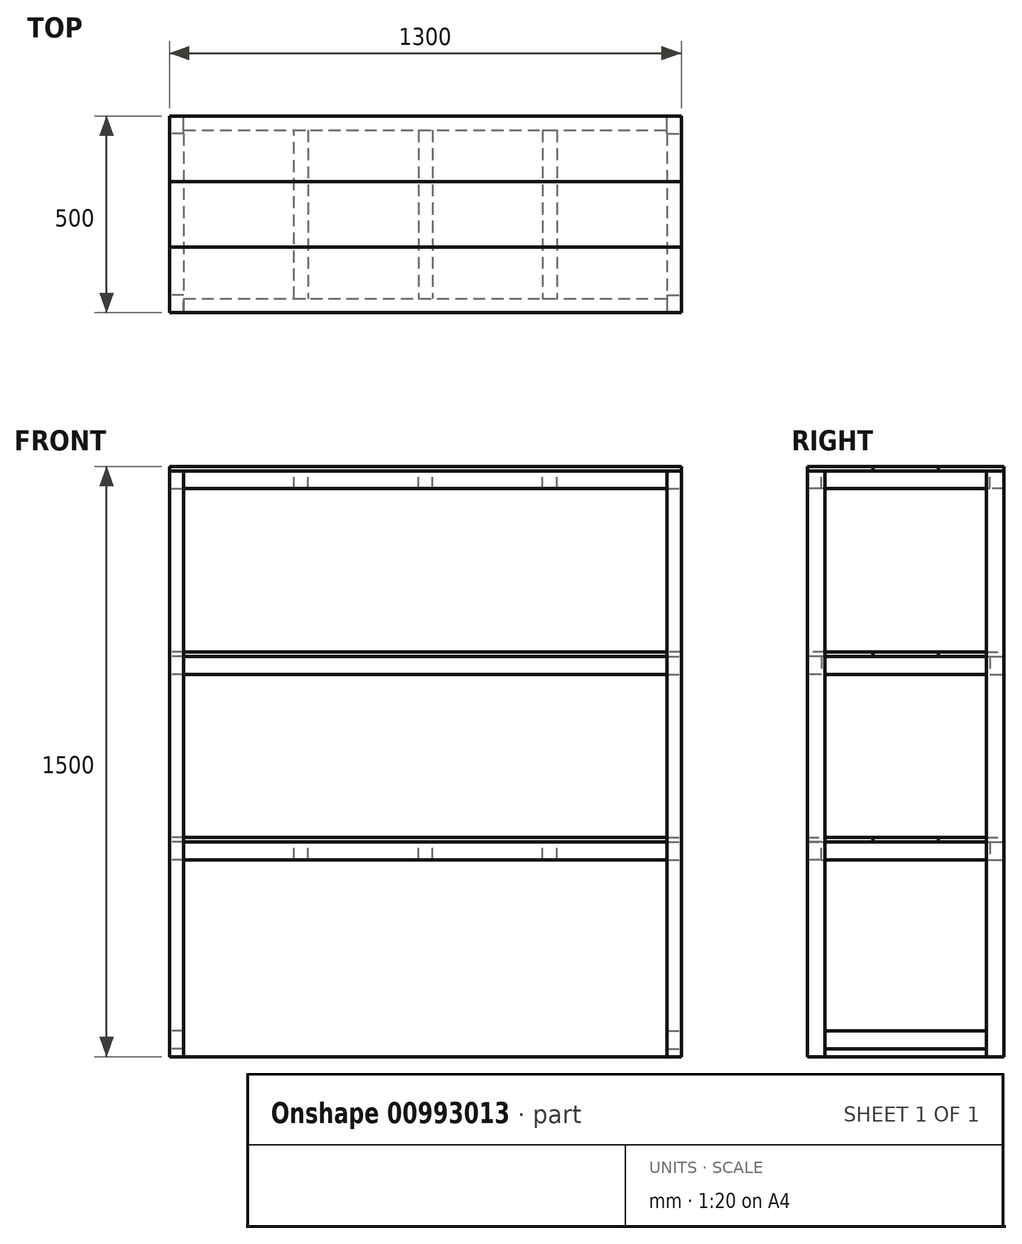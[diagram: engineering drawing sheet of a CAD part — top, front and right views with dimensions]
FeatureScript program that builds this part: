
annotation { "Feature Type Name" : "Feature", "Feature Type Description" : "" }
export const myFeature = defineFeature(function(context is Context, id is Id, definition is map)
    precondition{}
    {
        {
            assignVariable(context, id + "F0", {"name" : "h", "anyValue" : 1500});
        }
        {
            var Q0;
            Q0=qCreatedBy(makeId("Top.planeOp"),FACE);
            var sketch = newSketch(context, id + "F1", { "sketchPlane" : qUnion([Q0])});
            skLineSegment(sketch, "E0.bottom", {"start": v(650, 250) * mm, "end": v(-650, 250) * mm});
            skLineSegment(sketch, "E0.top", {"start": v(650, -250) * mm, "end": v(-650, -250) * mm});
            skLineSegment(sketch, "E0.left", {"start": v(650, 250) * mm, "end": v(650, -250) * mm});
            skLineSegment(sketch, "E0.right", {"start": v(-650, 250) * mm, "end": v(-650, -250) * mm});
            skPoint(sketch, "E0.middle", {"position": v(0, 0) * mm});
            skSolve(sketch);
        }
        {
            var Q0;
            Q0=makeQuery(id+"F1.imprint","IMPRINT",FACE,{"disambiguationData":[TD([[makeQuery(id+"F1.imprint","IMPRINT",EDGE,{"derivedFrom":sQuery(id+"F1.wireOp",EDGE,"E0.bottom")}),1.0]])]});
            extrude(context, id + "F2", {"entities" : qUnion([Q0]), "depth" : (getVariable(context, 'h')) * mm, "offsetDistance" : 25 * mm});
        }
        {
            var Q0;
            Q0=makeQuery(id+"F2.opExtrude","CAP_FACE",FACE,{"disambiguationData":[OSD([sQuery(id+"F1.wireOp",EDGE,"E0.bottom"),sQuery(id+"F1.wireOp",EDGE,"E0.top"),sQuery(id+"F1.wireOp",EDGE,"E0.left"),sQuery(id+"F1.wireOp",EDGE,"E0.right")])],"isStart":false});
            cPlane(context, id + "F3", {"entities" : qUnion([Q0]), "cplaneType" : CPlaneType.OFFSET, "offset" : 12 * mm, "oppositeDirection" : true, "width" : 150 * mm, "height" : 150 * mm});
        }
        {
            var Q0;
            Q0=makeQuery(id+"F2.opExtrude","CAP_FACE",FACE,{"disambiguationData":[OSD([sQuery(id+"F1.wireOp",EDGE,"E0.bottom"),sQuery(id+"F1.wireOp",EDGE,"E0.top"),sQuery(id+"F1.wireOp",EDGE,"E0.left"),sQuery(id+"F1.wireOp",EDGE,"E0.right")])],"isStart":true});
            var sketch = newSketch(context, id + "F4", { "sketchPlane" : qUnion([Q0])});
            skLineSegment(sketch, "E1.bottom", {"start": v(-650, 205) * mm, "end": v(-614, 205) * mm});
            skLineSegment(sketch, "E1.top", {"start": v(-650, 250) * mm, "end": v(-614, 250) * mm});
            skLineSegment(sketch, "E1.left", {"start": v(-650, 205) * mm, "end": v(-650, 250) * mm});
            skLineSegment(sketch, "E1.right", {"start": v(-614, 205) * mm, "end": v(-614, 250) * mm});
            skLineSegment(sketch, "E2.bottom", {"start": v(-650, -250) * mm, "end": v(-614, -250) * mm});
            skLineSegment(sketch, "E2.top", {"start": v(-650, -205) * mm, "end": v(-614, -205) * mm});
            skLineSegment(sketch, "E2.left", {"start": v(-650, -250) * mm, "end": v(-650, -205) * mm});
            skLineSegment(sketch, "E2.right", {"start": v(-614, -250) * mm, "end": v(-614, -205) * mm});
            skLineSegment(sketch, "E3.bottom", {"start": v(650, -250) * mm, "end": v(614, -250) * mm});
            skLineSegment(sketch, "E3.top", {"start": v(650, -205) * mm, "end": v(614, -205) * mm});
            skLineSegment(sketch, "E3.left", {"start": v(650, -250) * mm, "end": v(650, -205) * mm});
            skLineSegment(sketch, "E3.right", {"start": v(614, -250) * mm, "end": v(614, -205) * mm});
            skLineSegment(sketch, "E4.bottom", {"start": v(650, 250) * mm, "end": v(614, 250) * mm});
            skLineSegment(sketch, "E4.top", {"start": v(650, 205) * mm, "end": v(614, 205) * mm});
            skLineSegment(sketch, "E4.left", {"start": v(650, 250) * mm, "end": v(650, 205) * mm});
            skLineSegment(sketch, "E4.right", {"start": v(614, 250) * mm, "end": v(614, 205) * mm});
            skSolve(sketch);
        }
        {
            var Q0;
            Q0=makeQuery(id+"F4.imprint","IMPRINT",FACE,{"disambiguationData":[TD([[makeQuery(id+"F4.imprint","IMPRINT",EDGE,{"derivedFrom":sQuery(id+"F4.wireOp",EDGE,"E1.bottom")}),1.0]])]});
            var Q1;
            Q1=makeQuery(id+"F4.imprint","IMPRINT",FACE,{"disambiguationData":[TD([[makeQuery(id+"F4.imprint","IMPRINT",EDGE,{"derivedFrom":sQuery(id+"F4.wireOp",EDGE,"E2.bottom")}),-1.0]])]});
            var Q2;
            Q2=makeQuery(id+"F4.imprint","IMPRINT",FACE,{"disambiguationData":[TD([[makeQuery(id+"F4.imprint","IMPRINT",EDGE,{"derivedFrom":sQuery(id+"F4.wireOp",EDGE,"E4.bottom")}),1.0]])]});
            var Q3;
            Q3=makeQuery(id+"F4.imprint","IMPRINT",FACE,{"disambiguationData":[TD([[makeQuery(id+"F4.imprint","IMPRINT",EDGE,{"derivedFrom":sQuery(id+"F4.wireOp",EDGE,"E3.bottom")}),-1.0]])]});
            var Q4;
            Q4=qCreatedBy(id+"F3.planeOp",FACE);
            extrude(context, id + "F5", {"entities" : qUnion([Q0, Q1, Q2, Q3]), "endBound" : BoundingType.UP_TO_SURFACE, "oppositeDirection" : true, "depth" : (getVariable(context, 'h') - 12) * mm, "endBoundEntityFace" : qUnion([Q4]), "offsetDistance" : 25 * mm});
        }
        {
            var Q0;
            Q0=qCreatedBy(id+"F3.planeOp",FACE);
            var sketch = newSketch(context, id + "F6", { "sketchPlane" : qUnion([Q0])});
            skLineSegment(sketch, "E5.bottom", {"start": v(-650, 205) * mm, "end": v(-614, 205) * mm});
            skLineSegment(sketch, "E5.top", {"start": v(-650, -205) * mm, "end": v(-614, -205) * mm});
            skLineSegment(sketch, "E5.left", {"start": v(-650, 205) * mm, "end": v(-650, -205) * mm});
            skLineSegment(sketch, "E5.right", {"start": v(-614, 205) * mm, "end": v(-614, -205) * mm});
            skLineSegment(sketch, "E6.bottom", {"start": v(-614, 250) * mm, "end": v(614, 250) * mm});
            skLineSegment(sketch, "E6.top", {"start": v(-614, 214) * mm, "end": v(614, 214) * mm});
            skLineSegment(sketch, "E6.left", {"start": v(-614, 250) * mm, "end": v(-614, 214) * mm});
            skLineSegment(sketch, "E6.right", {"start": v(614, 250) * mm, "end": v(614, 214) * mm});
            skLineSegment(sketch, "E7.bottom", {"start": v(614, 205) * mm, "end": v(650, 205) * mm});
            skLineSegment(sketch, "E7.top", {"start": v(614, -205) * mm, "end": v(650, -205) * mm});
            skLineSegment(sketch, "E7.left", {"start": v(614, 205) * mm, "end": v(614, -205) * mm});
            skLineSegment(sketch, "E7.right", {"start": v(650, 205) * mm, "end": v(650, -205) * mm});
            skLineSegment(sketch, "E8.bottom", {"start": v(-614, -214) * mm, "end": v(614, -214) * mm});
            skLineSegment(sketch, "E8.top", {"start": v(-614, -250) * mm, "end": v(614, -250) * mm});
            skLineSegment(sketch, "E8.left", {"start": v(-614, -214) * mm, "end": v(-614, -250) * mm});
            skLineSegment(sketch, "E8.right", {"start": v(614, -214) * mm, "end": v(614, -250) * mm});
            skSolve(sketch);
        }
        {
            var Q0;
            Q0=makeQuery(id+"F6.imprint","IMPRINT",FACE,{"disambiguationData":[TD([[makeQuery(id+"F6.imprint","IMPRINT",EDGE,{"derivedFrom":sQuery(id+"F6.wireOp",EDGE,"E5.bottom")}),-1.0]])]});
            var Q1;
            Q1=makeQuery(id+"F6.imprint","IMPRINT",FACE,{"disambiguationData":[TD([[makeQuery(id+"F6.imprint","IMPRINT",EDGE,{"derivedFrom":sQuery(id+"F6.wireOp",EDGE,"E6.bottom")}),-1.0]])]});
            var Q2;
            Q2=makeQuery(id+"F6.imprint","IMPRINT",FACE,{"disambiguationData":[TD([[makeQuery(id+"F6.imprint","IMPRINT",EDGE,{"derivedFrom":sQuery(id+"F6.wireOp",EDGE,"E7.bottom")}),-1.0]])]});
            var Q3;
            Q3=makeQuery(id+"F6.imprint","IMPRINT",FACE,{"disambiguationData":[TD([[makeQuery(id+"F6.imprint","IMPRINT",EDGE,{"derivedFrom":sQuery(id+"F6.wireOp",EDGE,"E8.bottom")}),-1.0]])]});
            extrude(context, id + "F7", {"entities" : qUnion([Q0, Q1, Q2, Q3]), "oppositeDirection" : true, "depth" : 45 * mm, "offsetDistance" : 25 * mm});
        }
        {
            var Q0;
            Q0=qCreatedBy(id+"F3.planeOp",FACE);
            var sketch = newSketch(context, id + "F8", { "sketchPlane" : qUnion([Q0])});
            skLineSegment(sketch, "E9.bottom", {"start": v(-334, 214) * mm, "end": v(-298, 214) * mm});
            skLineSegment(sketch, "E9.top", {"start": v(-334, -214) * mm, "end": v(-298, -214) * mm});
            skLineSegment(sketch, "E9.left", {"start": v(-334, 214) * mm, "end": v(-334, -214) * mm});
            skLineSegment(sketch, "E9.right", {"start": v(-298, 214) * mm, "end": v(-298, -214) * mm});
            skLineSegment(sketch, "E10.bottom", {"start": v(-18, 214) * mm, "end": v(18, 214) * mm});
            skLineSegment(sketch, "E10.top", {"start": v(-18, -214) * mm, "end": v(18, -214) * mm});
            skLineSegment(sketch, "E10.left", {"start": v(-18, 214) * mm, "end": v(-18, -214) * mm});
            skLineSegment(sketch, "E10.right", {"start": v(18, 214) * mm, "end": v(18, -214) * mm});
            skLineSegment(sketch, "E11.bottom", {"start": v(298, 214) * mm, "end": v(334, 214) * mm});
            skLineSegment(sketch, "E11.top", {"start": v(298, -214) * mm, "end": v(334, -214) * mm});
            skLineSegment(sketch, "E11.left", {"start": v(298, 214) * mm, "end": v(298, -214) * mm});
            skLineSegment(sketch, "E11.right", {"start": v(334, 214) * mm, "end": v(334, -214) * mm});
            skSolve(sketch);
        }
        {
            var Q0;
            Q0=makeQuery(id+"F8.imprint","IMPRINT",FACE,{"disambiguationData":[TD([[makeQuery(id+"F8.imprint","IMPRINT",EDGE,{"derivedFrom":sQuery(id+"F8.wireOp",EDGE,"E9.bottom")}),-1.0]])]});
            var Q1;
            Q1=makeQuery(id+"F8.imprint","IMPRINT",FACE,{"disambiguationData":[TD([[makeQuery(id+"F8.imprint","IMPRINT",EDGE,{"derivedFrom":sQuery(id+"F8.wireOp",EDGE,"E10.bottom")}),-1.0]])]});
            var Q2;
            Q2=makeQuery(id+"F8.imprint","IMPRINT",FACE,{"disambiguationData":[TD([[makeQuery(id+"F8.imprint","IMPRINT",EDGE,{"derivedFrom":sQuery(id+"F8.wireOp",EDGE,"E11.bottom")}),-1.0]])]});
            extrude(context, id + "F9", {"entities" : qUnion([Q0, Q1, Q2]), "oppositeDirection" : true, "depth" : 45 * mm, "offsetDistance" : 25 * mm});
        }
        {
            var Q0;
            Q0=makeQuery(id+"F2.opExtrude","CAP_FACE",FACE,{"disambiguationData":[OSD([sQuery(id+"F1.wireOp",EDGE,"E0.bottom"),sQuery(id+"F1.wireOp",EDGE,"E0.top"),sQuery(id+"F1.wireOp",EDGE,"E0.left"),sQuery(id+"F1.wireOp",EDGE,"E0.right")])],"isStart":false});
            var sketch = newSketch(context, id + "F10", { "sketchPlane" : qUnion([Q0])});
            skLineSegment(sketch, "E12.bottom", {"start": v(-650, -83.33) * mm, "end": v(650, -83.33) * mm});
            skLineSegment(sketch, "E12.top", {"start": v(-650, -250) * mm, "end": v(650, -250) * mm});
            skLineSegment(sketch, "E12.left", {"start": v(-650, -83.33) * mm, "end": v(-650, -250) * mm});
            skLineSegment(sketch, "E12.right", {"start": v(650, -83.33) * mm, "end": v(650, -250) * mm});
            skLineSegment(sketch, "E13", {"start": v(-650, -83.33) * mm, "end": v(-650, 83.33) * mm});
            skLineSegment(sketch, "E14", {"start": v(-650, 83.33) * mm, "end": v(650, 83.33) * mm});
            skLineSegment(sketch, "E15", {"start": v(650, 83.33) * mm, "end": v(650, -83.33) * mm});
            skLineSegment(sketch, "E16", {"start": v(-650, 83.33) * mm, "end": v(-650, 250) * mm});
            skLineSegment(sketch, "E17", {"start": v(-650, 250) * mm, "end": v(650, 250) * mm});
            skLineSegment(sketch, "E18", {"start": v(650, 250) * mm, "end": v(650, 83.33) * mm});
            skSolve(sketch);
        }
        {
            var Q0;
            Q0=makeQuery(id+"F10.imprint","IMPRINT",FACE,{"disambiguationData":[TD([[makeQuery(id+"F10.imprint","IMPRINT",EDGE,{"derivedFrom":sQuery(id+"F10.wireOp",EDGE,"E12.bottom")}),-1.0]])]});
            extrude(context, id + "F11", {"entities" : qUnion([Q0]), "oppositeDirection" : true, "depth" : 12 * mm, "offsetDistance" : 25 * mm});
        }
        {
            var Q0;
            Q0=makeQuery(id+"F10.imprint","IMPRINT",FACE,{"disambiguationData":[TD([[makeQuery(id+"F10.imprint","IMPRINT",EDGE,{"derivedFrom":sQuery(id+"F10.wireOp",EDGE,"E12.bottom")}),1.0]])]});
            extrude(context, id + "F12", {"entities" : qUnion([Q0]), "oppositeDirection" : true, "depth" : 12 * mm, "offsetDistance" : 25 * mm});
        }
        {
            var Q0;
            Q0=makeQuery(id+"F10.imprint","IMPRINT",FACE,{"disambiguationData":[TD([[makeQuery(id+"F10.imprint","IMPRINT",EDGE,{"derivedFrom":sQuery(id+"F10.wireOp",EDGE,"E14")}),1.0]])]});
            extrude(context, id + "F13", {"entities" : qUnion([Q0]), "oppositeDirection" : true, "depth" : 12 * mm, "offsetDistance" : 25 * mm});
        }
        {
            var Q0;
            Q0=makeQuery(id+"F2.opExtrude","SWEPT_FACE",FACE,{"disambiguationData":[OSD([sQuery(id+"F1.wireOp",EDGE,"E0.top")])]});
            var sketch = newSketch(context, id + "F14", { "sketchPlane" : qUnion([Q0])});
            skLineSegment(sketch, "E19.bottom", {"start": v(-614, 545) * mm, "end": v(614, 545) * mm});
            skLineSegment(sketch, "E19.top", {"start": v(-614, 500) * mm, "end": v(614, 500) * mm});
            skLineSegment(sketch, "E19.left", {"start": v(-614, 545) * mm, "end": v(-614, 500) * mm});
            skLineSegment(sketch, "E19.right", {"start": v(614, 545) * mm, "end": v(614, 500) * mm});
            skSolve(sketch);
        }
        {
            var Q0;
            Q0=makeQuery(id+"F14.imprint","IMPRINT",FACE,{"disambiguationData":[TD([[makeQuery(id+"F14.imprint","IMPRINT",EDGE,{"derivedFrom":sQuery(id+"F14.wireOp",EDGE,"E19.bottom")}),-1.0]])]});
            extrude(context, id + "F15", {"entities" : qUnion([Q0]), "oppositeDirection" : true, "depth" : 36 * mm, "offsetDistance" : 25 * mm});
        }
        {
            var Q0;
            Q0=makeQuery(id+"F15.opExtrude","SWEPT_BODY",BODY,{"disambiguationData":[OSD([sQuery(id+"F14.wireOp",EDGE,"E19.bottom"),sQuery(id+"F14.wireOp",EDGE,"E19.top"),sQuery(id+"F14.wireOp",EDGE,"E19.left"),sQuery(id+"F14.wireOp",EDGE,"E19.right")])]});
            var Q1;
            Q1=qCreatedBy(makeId("Front.planeOp"),FACE);
            mirror(context, id + "F16", {"entities" : qUnion([Q0]), "mirrorPlane" : qUnion([Q1])});
        }
        {
            var Q0;
            Q0=makeQuery(id+"F2.opExtrude","SWEPT_FACE",FACE,{"disambiguationData":[OSD([sQuery(id+"F1.wireOp",EDGE,"E0.right")])]});
            var sketch = newSketch(context, id + "F17", { "sketchPlane" : qUnion([Q0])});
            skLineSegment(sketch, "E20.bottom", {"start": v(-205, 545) * mm, "end": v(205, 545) * mm});
            skLineSegment(sketch, "E20.top", {"start": v(-205, 500) * mm, "end": v(205, 500) * mm});
            skLineSegment(sketch, "E20.left", {"start": v(-205, 545) * mm, "end": v(-205, 500) * mm});
            skLineSegment(sketch, "E20.right", {"start": v(205, 545) * mm, "end": v(205, 500) * mm});
            skLineSegment(sketch, "E21.0", {"start": v(214, 500) * mm, "end": v(250, 500) * mm});
            skSolve(sketch);
        }
        {
            var Q0;
            Q0=makeQuery(id+"F17.imprint","IMPRINT",FACE,{"disambiguationData":[TD([[makeQuery(id+"F17.imprint","IMPRINT",EDGE,{"derivedFrom":sQuery(id+"F17.wireOp",EDGE,"E20.bottom")}),-1.0]])]});
            extrude(context, id + "F18", {"entities" : qUnion([Q0]), "oppositeDirection" : true, "depth" : 36 * mm, "offsetDistance" : 25 * mm});
        }
        {
            var Q0;
            Q0=makeQuery(id+"F18.opExtrude","SWEPT_BODY",BODY,{"disambiguationData":[OSD([sQuery(id+"F17.wireOp",EDGE,"E20.bottom"),sQuery(id+"F17.wireOp",EDGE,"E20.top"),sQuery(id+"F17.wireOp",EDGE,"E20.left"),sQuery(id+"F17.wireOp",EDGE,"E20.right")])]});
            var Q1;
            Q1=qCreatedBy(makeId("Right.planeOp"),FACE);
            mirror(context, id + "F19", {"entities" : qUnion([Q0]), "mirrorPlane" : qUnion([Q1])});
        }
        {
            var Q0;
            Q0=makeQuery(id+"F15.opExtrude","SWEPT_FACE",FACE,{"disambiguationData":[OSD([sQuery(id+"F14.wireOp",EDGE,"E19.bottom")])]});
            var sketch = newSketch(context, id + "F20", { "sketchPlane" : qUnion([Q0])});
            skLineSegment(sketch, "E22.0.0", {"start": v(-334, -214) * mm, "end": v(-334, 214) * mm});
            skLineSegment(sketch, "E22.0.1", {"start": v(-334, 214) * mm, "end": v(-298, 214) * mm});
            skLineSegment(sketch, "E22.0.2", {"start": v(-298, 214) * mm, "end": v(-298, -214) * mm});
            skLineSegment(sketch, "E22.0.3", {"start": v(-298, -214) * mm, "end": v(-334, -214) * mm});
            skLineSegment(sketch, "E23.0.0", {"start": v(-18, -214) * mm, "end": v(-18, 214) * mm});
            skLineSegment(sketch, "E23.0.1", {"start": v(-18, 214) * mm, "end": v(18, 214) * mm});
            skLineSegment(sketch, "E23.0.2", {"start": v(18, 214) * mm, "end": v(18, -214) * mm});
            skLineSegment(sketch, "E23.0.3", {"start": v(18, -214) * mm, "end": v(-18, -214) * mm});
            skLineSegment(sketch, "E24.0.0", {"start": v(298, -214) * mm, "end": v(298, 214) * mm});
            skLineSegment(sketch, "E24.0.1", {"start": v(298, 214) * mm, "end": v(334, 214) * mm});
            skLineSegment(sketch, "E24.0.2", {"start": v(334, 214) * mm, "end": v(334, -214) * mm});
            skLineSegment(sketch, "E24.0.3", {"start": v(334, -214) * mm, "end": v(298, -214) * mm});
            skSolve(sketch);
        }
        {
            var Q0;
            Q0=makeQuery(id+"F20.imprint","IMPRINT",FACE,{"disambiguationData":[TD([[makeQuery(id+"F20.imprint","IMPRINT",EDGE,{"derivedFrom":sQuery(id+"F20.wireOp",EDGE,"E22.0.0")}),-1.0]])]});
            var Q1;
            Q1=makeQuery(id+"F20.imprint","IMPRINT",FACE,{"disambiguationData":[TD([[makeQuery(id+"F20.imprint","IMPRINT",EDGE,{"derivedFrom":sQuery(id+"F20.wireOp",EDGE,"E23.0.0")}),-1.0]])]});
            var Q2;
            Q2=makeQuery(id+"F20.imprint","IMPRINT",FACE,{"disambiguationData":[TD([[makeQuery(id+"F20.imprint","IMPRINT",EDGE,{"derivedFrom":sQuery(id+"F20.wireOp",EDGE,"E24.0.0")}),-1.0]])]});
            extrude(context, id + "F21", {"entities" : qUnion([Q0, Q1, Q2]), "oppositeDirection" : true, "depth" : 45 * mm, "offsetDistance" : 25 * mm});
        }
        {
            var Q0;
            Q0=makeQuery(id+"F15.opExtrude","SWEPT_FACE",FACE,{"disambiguationData":[OSD([sQuery(id+"F14.wireOp",EDGE,"E19.bottom")])]});
            var sketch = newSketch(context, id + "F22", { "sketchPlane" : qUnion([Q0])});
            skLineSegment(sketch, "E25.0.0", {"start": v(650, -83.33) * mm, "end": v(-650, -83.33) * mm});
            skLineSegment(sketch, "E25.0.1", {"start": v(-650, -83.33) * mm, "end": v(-650, -250) * mm});
            skLineSegment(sketch, "E25.0.2", {"start": v(-650, -250) * mm, "end": v(650, -250) * mm});
            skLineSegment(sketch, "E25.0.3", {"start": v(650, -250) * mm, "end": v(650, -83.33) * mm});
            skLineSegment(sketch, "E26.0.0", {"start": v(650, 83.33) * mm, "end": v(-650, 83.33) * mm});
            skLineSegment(sketch, "E26.0.1", {"start": v(-650, 83.33) * mm, "end": v(-650, -83.33) * mm});
            skLineSegment(sketch, "E26.0.2", {"start": v(-650, -83.33) * mm, "end": v(650, -83.33) * mm});
            skLineSegment(sketch, "E26.0.3", {"start": v(650, -83.33) * mm, "end": v(650, 83.33) * mm});
            skLineSegment(sketch, "E27.0.0", {"start": v(-650, 250) * mm, "end": v(-650, 83.33) * mm});
            skLineSegment(sketch, "E27.0.1", {"start": v(-650, 83.33) * mm, "end": v(650, 83.33) * mm});
            skLineSegment(sketch, "E27.0.2", {"start": v(650, 83.33) * mm, "end": v(650, 250) * mm});
            skLineSegment(sketch, "E27.0.3", {"start": v(650, 250) * mm, "end": v(-650, 250) * mm});
            skSolve(sketch);
        }
        {
            var Q0;
            {var subQ5=sQuery(id+"F22.wireOp",EDGE,"E25.0.1");Q0=makeQuery(id+"F22.imprint","IMPRINT",FACE,{"disambiguationData":[TD([[makeQuery(id+"F22.imprint","IMPRINT",EDGE,{"derivedFrom":subQ5}),1.0]])]});}
            var Q1;
            {var subQ1=sQuery(id+"F14.wireOp",EDGE,"E19.bottom");Q1=makeQuery(id+"F22.imprint","IMPRINT",FACE,{"disambiguationData":[TD([[makeQuery(id+"F22.imprint","IMPRINT",EDGE,{"derivedFrom":makeQuery(id+"F15.opExtrude","CAP_EDGE",EDGE,{"disambiguationData":[OSD([subQ1])],"isStart":false})}),-1.0]])]});}
            extrude(context, id + "F23", {"entities" : qUnion([Q0, Q1]), "depth" : 12 * mm, "offsetDistance" : 25 * mm});
        }
        {
            var Q0;
            Q0=makeQuery(id+"F22.imprint","IMPRINT",FACE,{"disambiguationData":[TD([[makeQuery(id+"F22.imprint","IMPRINT",EDGE,{"derivedFrom":sQuery(id+"F22.wireOp",EDGE,"E26.0.1")}),1.0]])]});
            extrude(context, id + "F24", {"entities" : qUnion([Q0]), "depth" : 12 * mm, "offsetDistance" : 25 * mm});
        }
        {
            var Q0;
            Q0=makeQuery(id+"F22.imprint","IMPRINT",FACE,{"disambiguationData":[TD([[makeQuery(id+"F22.imprint","IMPRINT",EDGE,{"derivedFrom":sQuery(id+"F22.wireOp",EDGE,"E27.0.0")}),1.0]])]});
            extrude(context, id + "F25", {"entities" : qUnion([Q0]), "depth" : 12 * mm, "offsetDistance" : 25 * mm});
        }
        {
            var Q0;
            Q0=makeQuery(id+"F5.opExtrude","SWEPT_BODY",BODY,{"disambiguationData":[OSD([sQuery(id+"F4.wireOp",EDGE,"E1.bottom"),sQuery(id+"F4.wireOp",EDGE,"E1.top"),sQuery(id+"F4.wireOp",EDGE,"E1.left"),sQuery(id+"F4.wireOp",EDGE,"E1.right")])]});
            var Q1;
            Q1=makeQuery(id+"F5.opExtrude","SWEPT_BODY",BODY,{"disambiguationData":[OSD([sQuery(id+"F4.wireOp",EDGE,"E4.bottom"),sQuery(id+"F4.wireOp",EDGE,"E4.top"),sQuery(id+"F4.wireOp",EDGE,"E4.left"),sQuery(id+"F4.wireOp",EDGE,"E4.right")])]});
            var Q2;
            Q2=makeQuery(id+"F23.opExtrude","SWEPT_BODY",BODY,{"disambiguationData":[OSD([sQuery(id+"F22.wireOp",EDGE,"E25.0.1"),sQuery(id+"F22.wireOp",EDGE,"E25.0.2"),sQuery(id+"F22.wireOp",EDGE,"E25.0.3"),sQuery(id+"F22.wireOp",EDGE,"E26.0.2")])]});
            booleanBodies(context, id + "F26", {"operationType" : BooleanOperationType.SUBTRACTION, "tools" : qUnion([Q0, Q1]), "targets" : qUnion([Q2]), "keepTools" : true});
        }
        {
            var Q0;
            Q0=makeQuery(id+"F5.opExtrude","SWEPT_BODY",BODY,{"disambiguationData":[OSD([sQuery(id+"F4.wireOp",EDGE,"E2.bottom"),sQuery(id+"F4.wireOp",EDGE,"E2.top"),sQuery(id+"F4.wireOp",EDGE,"E2.left"),sQuery(id+"F4.wireOp",EDGE,"E2.right")])]});
            var Q1;
            Q1=makeQuery(id+"F5.opExtrude","SWEPT_BODY",BODY,{"disambiguationData":[OSD([sQuery(id+"F4.wireOp",EDGE,"E3.bottom"),sQuery(id+"F4.wireOp",EDGE,"E3.top"),sQuery(id+"F4.wireOp",EDGE,"E3.left"),sQuery(id+"F4.wireOp",EDGE,"E3.right")])]});
            var Q2;
            Q2=makeQuery(id+"F25.opExtrude","SWEPT_BODY",BODY,{"disambiguationData":[OSD([sQuery(id+"F22.wireOp",EDGE,"E27.0.0"),sQuery(id+"F22.wireOp",EDGE,"E27.0.1"),sQuery(id+"F22.wireOp",EDGE,"E27.0.2"),sQuery(id+"F22.wireOp",EDGE,"E27.0.3")])]});
            booleanBodies(context, id + "F27", {"operationType" : BooleanOperationType.SUBTRACTION, "tools" : qUnion([Q0, Q1]), "targets" : qUnion([Q2]), "keepTools" : true});
        }
        {
            var Q0;
            Q0=makeQuery(id+"F2.opExtrude","SWEPT_FACE",FACE,{"disambiguationData":[OSD([sQuery(id+"F1.wireOp",EDGE,"E0.right")])]});
            var sketch = newSketch(context, id + "F28", { "sketchPlane" : qUnion([Q0])});
            skLineSegment(sketch, "E28.bottom", {"start": v(-205, 65) * mm, "end": v(205, 65) * mm});
            skLineSegment(sketch, "E28.top", {"start": v(-205, 20) * mm, "end": v(205, 20) * mm});
            skLineSegment(sketch, "E28.left", {"start": v(-205, 65) * mm, "end": v(-205, 20) * mm});
            skLineSegment(sketch, "E28.right", {"start": v(205, 65) * mm, "end": v(205, 20) * mm});
            skSolve(sketch);
        }
        {
            var Q0;
            Q0=makeQuery(id+"F28.imprint","IMPRINT",FACE,{"disambiguationData":[TD([[makeQuery(id+"F28.imprint","IMPRINT",EDGE,{"derivedFrom":sQuery(id+"F28.wireOp",EDGE,"E28.bottom")}),-1.0]])]});
            extrude(context, id + "F29", {"entities" : qUnion([Q0]), "oppositeDirection" : true, "depth" : 36 * mm, "offsetDistance" : 25 * mm});
        }
        {
            var Q0;
            Q0=makeQuery(id+"F29.opExtrude","SWEPT_BODY",BODY,{"disambiguationData":[OSD([sQuery(id+"F28.wireOp",EDGE,"E28.bottom"),sQuery(id+"F28.wireOp",EDGE,"E28.top"),sQuery(id+"F28.wireOp",EDGE,"E28.left"),sQuery(id+"F28.wireOp",EDGE,"E28.right")])]});
            var Q1;
            Q1=qCreatedBy(makeId("Right.planeOp"),FACE);
            mirror(context, id + "F30", {"entities" : qUnion([Q0]), "mirrorPlane" : qUnion([Q1])});
        }
        {
            var Q0;
            Q0=makeQuery(id+"F2.opExtrude","SWEPT_FACE",FACE,{"disambiguationData":[OSD([sQuery(id+"F1.wireOp",EDGE,"E0.top")])]});
            var sketch = newSketch(context, id + "F31", { "sketchPlane" : qUnion([Q0])});
            skLineSegment(sketch, "E29.bottom", {"start": v(-614, 1016.5) * mm, "end": v(614, 1016.5) * mm});
            skLineSegment(sketch, "E29.top", {"start": v(-614, 971.5) * mm, "end": v(614, 971.5) * mm});
            skLineSegment(sketch, "E29.left", {"start": v(-614, 1016.5) * mm, "end": v(-614, 971.5) * mm});
            skLineSegment(sketch, "E29.right", {"start": v(614, 1016.5) * mm, "end": v(614, 971.5) * mm});
            skLineSegment(sketch, "E30", {"start": v(-614, 1016.5) * mm, "end": v(-614, 1028.5) * mm, "construction": true});
            skLineSegment(sketch, "E31", {"start": v(-614, 1028.5) * mm, "end": v(614, 1028.5) * mm, "construction": true});
            skLineSegment(sketch, "E32", {"start": v(614, 1028.5) * mm, "end": v(614, 1016.5) * mm, "construction": true});
            skLineSegment(sketch, "E33", {"start": v(0, 1443) * mm, "end": v(0, 1028.5) * mm, "construction": true});
            skLineSegment(sketch, "E34", {"start": v(0, 971.5) * mm, "end": v(0, 557) * mm, "construction": true});
            skSolve(sketch);
        }
        {
            var Q0;
            Q0=makeQuery(id+"F31.imprint","IMPRINT",FACE,{"disambiguationData":[TD([[makeQuery(id+"F31.imprint","IMPRINT",EDGE,{"derivedFrom":sQuery(id+"F31.wireOp",EDGE,"E29.bottom")}),-1.0]])]});
            extrude(context, id + "F32", {"entities" : qUnion([Q0]), "oppositeDirection" : true, "depth" : 36 * mm, "offsetDistance" : 25 * mm});
        }
        {
            var Q0;
            Q0=makeQuery(id+"F32.opExtrude","SWEPT_BODY",BODY,{"disambiguationData":[OSD([sQuery(id+"F31.wireOp",EDGE,"E29.bottom"),sQuery(id+"F31.wireOp",EDGE,"E29.top"),sQuery(id+"F31.wireOp",EDGE,"E29.left"),sQuery(id+"F31.wireOp",EDGE,"E29.right")])]});
            var Q1;
            Q1=qCreatedBy(makeId("Front.planeOp"),FACE);
            mirror(context, id + "F33", {"entities" : qUnion([Q0]), "mirrorPlane" : qUnion([Q1])});
        }
        {
            var Q0;
            Q0=makeQuery(id+"F2.opExtrude","SWEPT_FACE",FACE,{"disambiguationData":[OSD([sQuery(id+"F1.wireOp",EDGE,"E0.right")])]});
            var sketch = newSketch(context, id + "F34", { "sketchPlane" : qUnion([Q0])});
            skLineSegment(sketch, "E35.0", {"start": v(214, 971.5) * mm, "end": v(250, 971.5) * mm});
            skLineSegment(sketch, "E36.bottom", {"start": v(-205, 1016.5) * mm, "end": v(205, 1016.5) * mm});
            skLineSegment(sketch, "E36.top", {"start": v(-205, 971.5) * mm, "end": v(205, 971.5) * mm});
            skLineSegment(sketch, "E36.left", {"start": v(-205, 1016.5) * mm, "end": v(-205, 971.5) * mm});
            skLineSegment(sketch, "E36.right", {"start": v(205, 1016.5) * mm, "end": v(205, 971.5) * mm});
            skSolve(sketch);
        }
        {
            var Q0;
            Q0=makeQuery(id+"F34.imprint","IMPRINT",FACE,{"disambiguationData":[TD([[makeQuery(id+"F34.imprint","IMPRINT",EDGE,{"derivedFrom":sQuery(id+"F34.wireOp",EDGE,"E36.bottom")}),-1.0]])]});
            extrude(context, id + "F35", {"entities" : qUnion([Q0]), "oppositeDirection" : true, "depth" : 36 * mm, "offsetDistance" : 25 * mm});
        }
        {
            var Q0;
            Q0=makeQuery(id+"F35.opExtrude","SWEPT_BODY",BODY,{"disambiguationData":[OSD([sQuery(id+"F34.wireOp",EDGE,"E36.bottom"),sQuery(id+"F34.wireOp",EDGE,"E36.top"),sQuery(id+"F34.wireOp",EDGE,"E36.left"),sQuery(id+"F34.wireOp",EDGE,"E36.right")])]});
            var Q1;
            Q1=qCreatedBy(makeId("Right.planeOp"),FACE);
            mirror(context, id + "F36", {"entities" : qUnion([Q0]), "mirrorPlane" : qUnion([Q1])});
        }
        {
            var Q0;
            Q0=makeQuery(id+"F32.opExtrude","SWEPT_FACE",FACE,{"disambiguationData":[OSD([sQuery(id+"F31.wireOp",EDGE,"E29.bottom")])]});
            var sketch = newSketch(context, id + "F37", { "sketchPlane" : qUnion([Q0])});
            skLineSegment(sketch, "E37.0.0", {"start": v(-650, -205) * mm, "end": v(-614, -205) * mm});
            skLineSegment(sketch, "E37.0.1", {"start": v(-614, -205) * mm, "end": v(-614, -250) * mm});
            skLineSegment(sketch, "E37.0.2", {"start": v(-614, -250) * mm, "end": v(614, -250) * mm});
            skLineSegment(sketch, "E37.0.3", {"start": v(614, -250) * mm, "end": v(614, -205) * mm});
            skLineSegment(sketch, "E37.0.4", {"start": v(614, -205) * mm, "end": v(650, -205) * mm});
            skLineSegment(sketch, "E37.0.5", {"start": v(650, -205) * mm, "end": v(650, -83.33) * mm});
            skLineSegment(sketch, "E37.0.6", {"start": v(650, -83.33) * mm, "end": v(-650, -83.33) * mm});
            skLineSegment(sketch, "E37.0.7", {"start": v(-650, -83.33) * mm, "end": v(-650, -205) * mm});
            skLineSegment(sketch, "E38.0.0", {"start": v(650, 83.33) * mm, "end": v(-650, 83.33) * mm});
            skLineSegment(sketch, "E38.0.1", {"start": v(-650, 83.33) * mm, "end": v(-650, -83.33) * mm});
            skLineSegment(sketch, "E38.0.2", {"start": v(-650, -83.33) * mm, "end": v(650, -83.33) * mm});
            skLineSegment(sketch, "E38.0.3", {"start": v(650, -83.33) * mm, "end": v(650, 83.33) * mm});
            skLineSegment(sketch, "E39.0.0", {"start": v(-614, 250) * mm, "end": v(-614, 205) * mm});
            skLineSegment(sketch, "E39.0.1", {"start": v(-614, 205) * mm, "end": v(-650, 205) * mm});
            skLineSegment(sketch, "E39.0.2", {"start": v(-650, 205) * mm, "end": v(-650, 83.33) * mm});
            skLineSegment(sketch, "E39.0.3", {"start": v(-650, 83.33) * mm, "end": v(650, 83.33) * mm});
            skLineSegment(sketch, "E39.0.4", {"start": v(650, 83.33) * mm, "end": v(650, 205) * mm});
            skLineSegment(sketch, "E39.0.5", {"start": v(650, 205) * mm, "end": v(614, 205) * mm});
            skLineSegment(sketch, "E39.0.6", {"start": v(614, 205) * mm, "end": v(614, 250) * mm});
            skLineSegment(sketch, "E39.0.7", {"start": v(614, 250) * mm, "end": v(-614, 250) * mm});
            skSolve(sketch);
        }
        {
            var Q0;
            {var subQ4=sQuery(id+"F37.wireOp",EDGE,"E37.0.0");Q0=makeQuery(id+"F37.imprint","IMPRINT",FACE,{"disambiguationData":[TD([[makeQuery(id+"F37.imprint","IMPRINT",EDGE,{"derivedFrom":subQ4}),1.0]])]});}
            var Q1;
            {var subQ0=sQuery(id+"F37.wireOp",EDGE,"E37.0.2");Q1=makeQuery(id+"F37.imprint","IMPRINT",FACE,{"disambiguationData":[TD([[makeQuery(id+"F37.imprint","IMPRINT",EDGE,{"derivedFrom":subQ0}),1.0]])]});}
            extrude(context, id + "F38", {"entities" : qUnion([Q0, Q1]), "depth" : 12 * mm, "offsetDistance" : 25 * mm});
        }
        {
            var Q0;
            Q0=makeQuery(id+"F37.imprint","IMPRINT",FACE,{"disambiguationData":[TD([[makeQuery(id+"F37.imprint","IMPRINT",EDGE,{"derivedFrom":sQuery(id+"F37.wireOp",EDGE,"E38.0.1")}),1.0]])]});
            extrude(context, id + "F39", {"entities" : qUnion([Q0]), "depth" : 12 * mm, "offsetDistance" : 25 * mm});
        }
        {
            var Q0;
            Q0=makeQuery(id+"F37.imprint","IMPRINT",FACE,{"disambiguationData":[TD([[makeQuery(id+"F37.imprint","IMPRINT",EDGE,{"derivedFrom":sQuery(id+"F37.wireOp",EDGE,"E39.0.0")}),1.0]])]});
            extrude(context, id + "F40", {"entities" : qUnion([Q0]), "depth" : 12 * mm, "offsetDistance" : 25 * mm});
        }
    });
